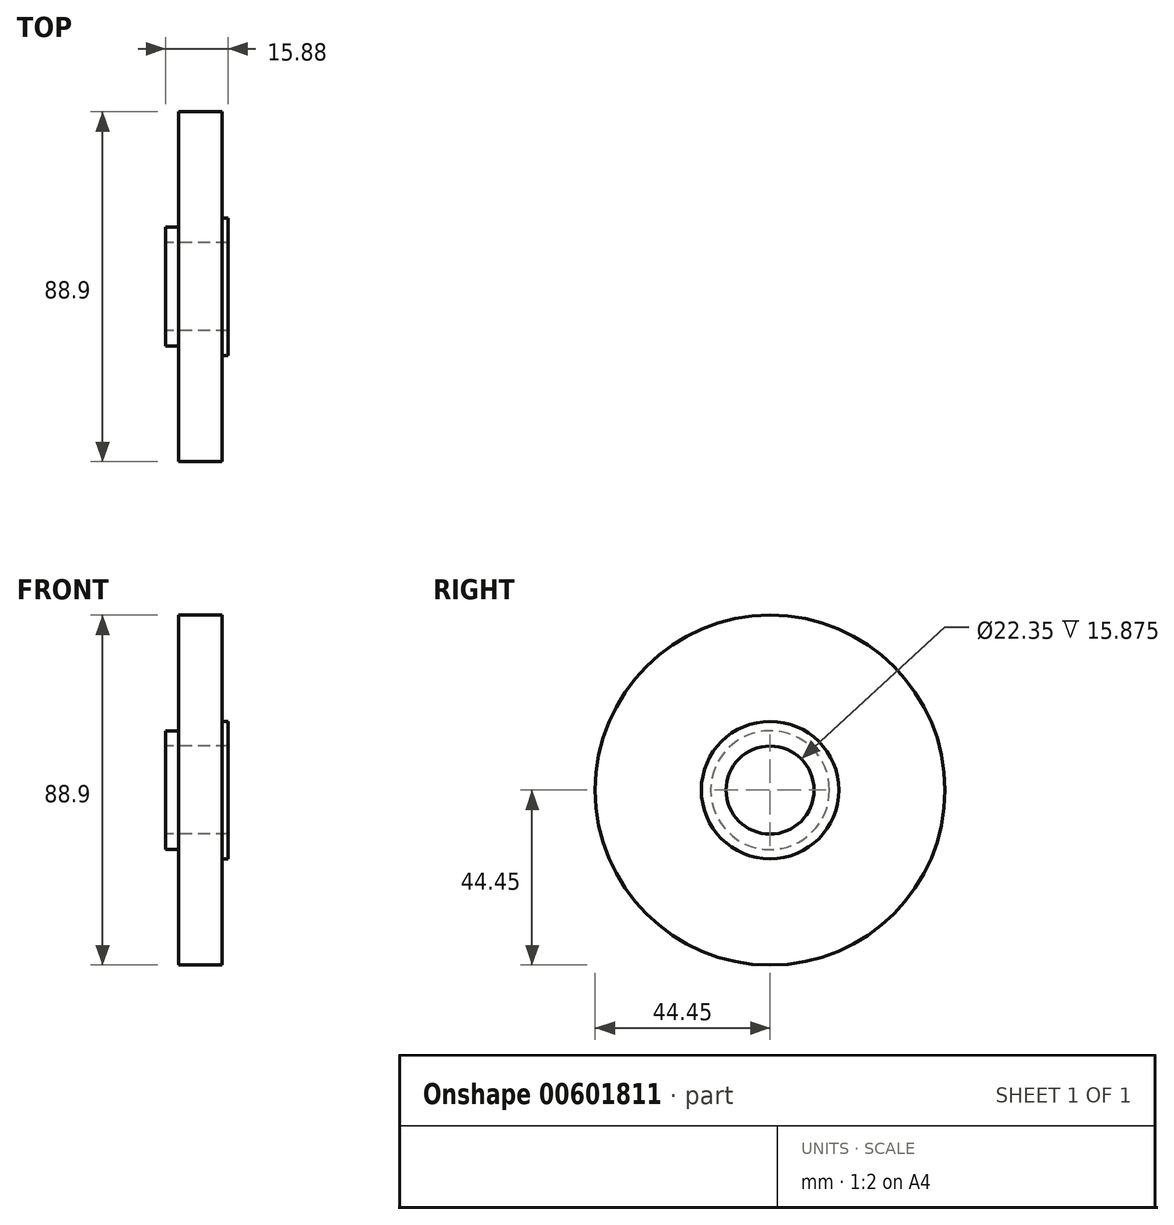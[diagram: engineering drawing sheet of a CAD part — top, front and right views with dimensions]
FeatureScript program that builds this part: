
annotation { "Feature Type Name" : "Feature", "Feature Type Description" : "" }
export const myFeature = defineFeature(function(context is Context, id is Id, definition is map)
    precondition{}
    {
        {
            var Q0;
            Q0=qCreatedBy(makeId("Front.planeOp"),FACE);
            var sketch = newSketch(context, id + "F0", { "sketchPlane" : qUnion([Q0])});
            skLineSegment(sketch, "E0", {"start": v(-24.08, 0) * mm, "end": v(27.52, 0) * mm, "construction": true});
            skLineSegment(sketch, "E1", {"start": v(0, 11.18) * mm, "end": v(15.87, 11.18) * mm});
            skLineSegment(sketch, "E2", {"start": v(15.88, 11.18) * mm, "end": v(15.88, 17.46) * mm});
            skLineSegment(sketch, "E3", {"start": v(15.88, 17.46) * mm, "end": v(14.35, 17.46) * mm});
            skLineSegment(sketch, "E4", {"start": v(14.35, 17.46) * mm, "end": v(14.35, 44.45) * mm});
            skLineSegment(sketch, "E5", {"start": v(14.35, 44.45) * mm, "end": v(3.25, 44.45) * mm});
            skLineSegment(sketch, "E6", {"start": v(3.25, 44.45) * mm, "end": v(3.25, 15.09) * mm});
            skLineSegment(sketch, "E7", {"start": v(3.25, 15.09) * mm, "end": v(0, 15.09) * mm});
            skLineSegment(sketch, "E8", {"start": v(0, 15.09) * mm, "end": v(0, 11.18) * mm});
            skSolve(sketch);
        }
        {
            var Q0;
            Q0 = qSketchRegion(id + "F0", true);
            var Q1;
            Q1=sQuery(id+"F0.wireOp",EDGE,"E0");
            revolve(context, id + "F1", {"entities" : qUnion([Q0]), "axis" : qUnion([Q1]), "revolveType" : RevolveType.FULL});
        }
    });
